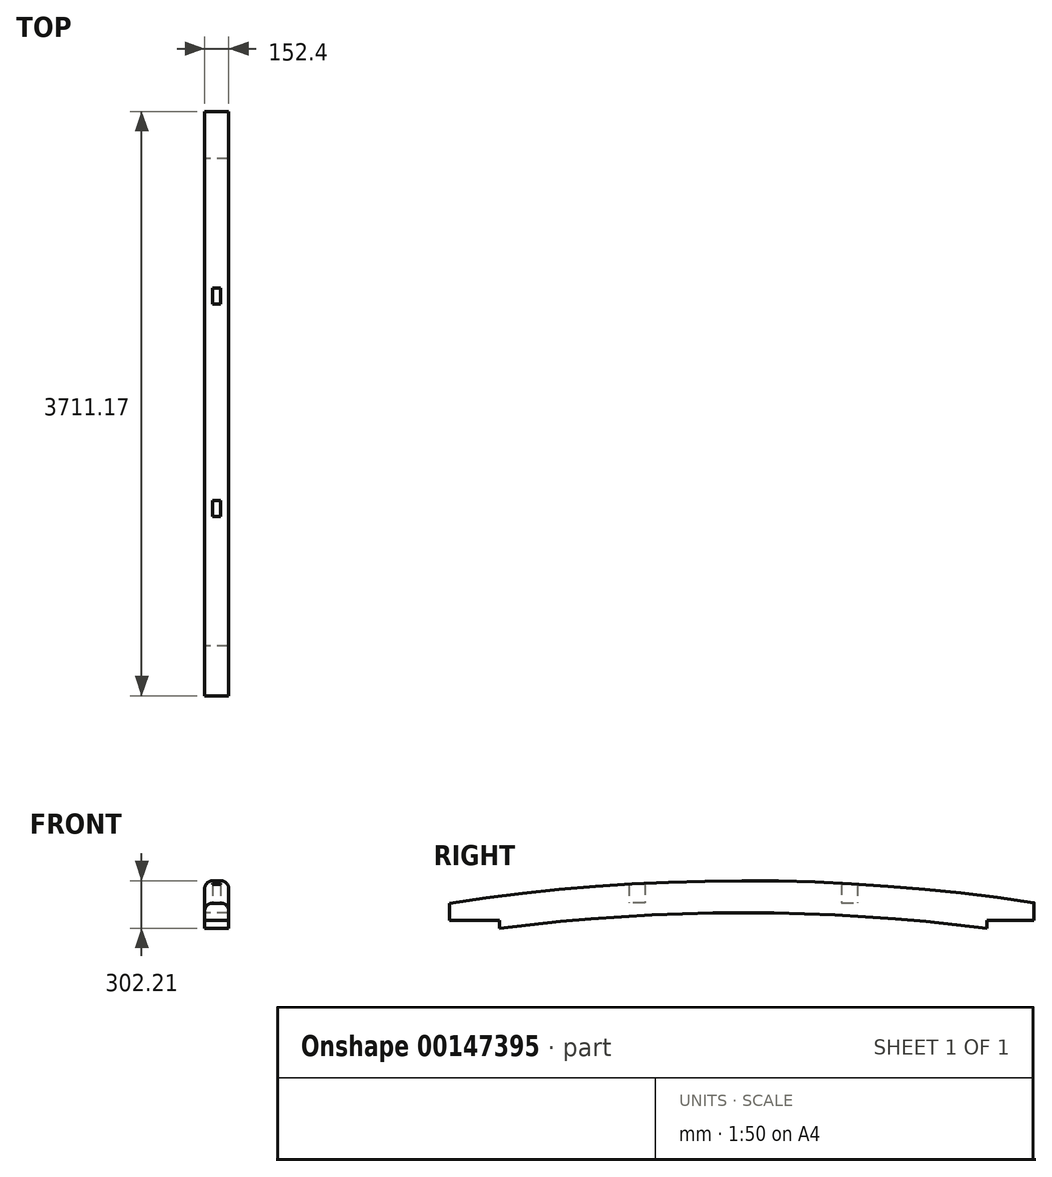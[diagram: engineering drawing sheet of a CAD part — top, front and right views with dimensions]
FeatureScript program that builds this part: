
annotation { "Feature Type Name" : "Feature", "Feature Type Description" : "" }
export const myFeature = defineFeature(function(context is Context, id is Id, definition is map)
    precondition{}
    {
        {
            var Q0;
            Q0=qCreatedBy(makeId("Right.planeOp"),FACE);
            var sketch = newSketch(context, id + "F0", { "sketchPlane" : qUnion([Q0])});
            skLineSegment(sketch, "E0", {"start": v(-1546.8, 0) * mm, "end": v(1546.8, 0) * mm, "construction": true});
            skLineSegment(sketch, "E1.bottom", {"start": v(1546.8, 0) * mm, "end": v(1750, 0) * mm, "construction": true});
            skLineSegment(sketch, "E1.top", {"start": v(1546.8, -203.2) * mm, "end": v(1750, -203.2) * mm, "construction": true});
            skLineSegment(sketch, "E1.left", {"start": v(1546.8, 0) * mm, "end": v(1546.8, -203.2) * mm, "construction": true});
            skLineSegment(sketch, "E1.right", {"start": v(1750, 0) * mm, "end": v(1750, -203.2) * mm, "construction": true});
            skLineSegment(sketch, "E2.bottom", {"start": v(-1546.8, 0) * mm, "end": v(-1750, 0) * mm, "construction": true});
            skLineSegment(sketch, "E2.top", {"start": v(-1546.8, -203.2) * mm, "end": v(-1750, -203.2) * mm, "construction": true});
            skLineSegment(sketch, "E2.left", {"start": v(-1546.8, 0) * mm, "end": v(-1546.8, -203.2) * mm, "construction": true});
            skLineSegment(sketch, "E2.right", {"start": v(-1750, 0) * mm, "end": v(-1750, -203.2) * mm, "construction": true});
            skLineSegment(sketch, "E3.0", {"start": v(-1546.8, -50) * mm, "end": v(1546.8, -50) * mm, "construction": true});
            skArc(sketch, "E4", {"start": v(1546.8, -50) * mm, "mid": v(0, 49.01) * mm, "end": v(-1546.8, -50) * mm});
            skArc(sketch, "E5.0", {"start": v(1846.2, 113.27) * mm, "mid": v(-9.5, 252.2) * mm, "end": v(-1864.97, 110.41) * mm});
            skLineSegment(sketch, "E6", {"start": v(1546.8, -50) * mm, "end": v(1546.8, 0) * mm});
            skLineSegment(sketch, "E7", {"start": v(1846.2, 0) * mm, "end": v(1846.2, 113.27) * mm});
            skLineSegment(sketch, "E8", {"start": v(1846.2, 0) * mm, "end": v(1546.8, 0) * mm});
            skLineSegment(sketch, "E9", {"start": v(-1546.8, -50) * mm, "end": v(-1546.8, 0) * mm});
            skLineSegment(sketch, "E10", {"start": v(-1864.97, 0) * mm, "end": v(-1546.8, 0) * mm});
            skLineSegment(sketch, "E11", {"start": v(-1864.97, 0) * mm, "end": v(-1864.97, 110.41) * mm});
            skLineSegment(sketch, "E12", {"start": v(0, 0) * mm, "end": v(0, -260.57) * mm, "construction": true});
            skSolve(sketch);
        }
        {
            var Q0;
            Q0=makeQuery(id+"F0.imprint","IMPRINT",FACE,{"disambiguationData":[TD([[makeQuery(id+"F0.imprint","IMPRINT",EDGE,{"derivedFrom":sQuery(id+"F0.wireOp",EDGE,"E4")}),-1.0]])]});
            extrude(context, id + "F1", {"entities" : qUnion([Q0]), "depth" : 152.4 * mm});
        }
        {
            var Q0;
            Q0=makeQuery(id+"F1.opExtrude","CAP_EDGE",EDGE,{"disambiguationData":[OSD([sQuery(id+"F0.wireOp",EDGE,"E5.0")])],"isStart":false});
            var Q1;
            Q1=makeQuery(id+"F1.opExtrude","CAP_EDGE",EDGE,{"disambiguationData":[OSD([sQuery(id+"F0.wireOp",EDGE,"E5.0")])],"isStart":true});
            fillet(context, id + "F2", {"entities" : qUnion([Q0, Q1]), "radius" : 50 * mm, "tangentPropagation" : true, "allowEdgeOverflow" : false});
        }
        {
            var Q0;
            {var subQ0=sQuery(id+"F0.wireOp",EDGE,"E5.0");Q0=makeQuery(id+"F2.opFillet","BLEND_VERTEX",VERTEX,{"blendedFrom":[makeQuery(id+"F1.opExtrude","CAP_EDGE",EDGE,{"disambiguationData":[OSD([subQ0])],"isStart":true}),makeQuery(id+"F1.opExtrude","SWEPT_FACE",FACE,{"disambiguationData":[OSD([subQ0])]}),makeQuery(id+"F1.opExtrude","SWEPT_FACE",FACE,{"disambiguationData":[OSD([sQuery(id+"F0.wireOp",EDGE,"E7")])]})],"blendedInto":[makeQuery(id+"F1.opExtrude","SWEPT_FACE",FACE,{"disambiguationData":[OSD([subQ0])]}),makeQuery(id+"F1.opExtrude","SWEPT_FACE",FACE,{"disambiguationData":[OSD([sQuery(id+"F0.wireOp",EDGE,"E7")])]})]});}
            var Q1;
            {var subQ0=sQuery(id+"F0.wireOp",EDGE,"E5.0");Q1=makeQuery(id+"F2.opFillet","BLEND_VERTEX",VERTEX,{"blendedFrom":[makeQuery(id+"F1.opExtrude","CAP_EDGE",EDGE,{"disambiguationData":[OSD([subQ0])],"isStart":false}),makeQuery(id+"F1.opExtrude","SWEPT_FACE",FACE,{"disambiguationData":[OSD([subQ0])]}),makeQuery(id+"F1.opExtrude","SWEPT_FACE",FACE,{"disambiguationData":[OSD([sQuery(id+"F0.wireOp",EDGE,"E7")])]})],"blendedInto":[makeQuery(id+"F1.opExtrude","SWEPT_FACE",FACE,{"disambiguationData":[OSD([subQ0])]}),makeQuery(id+"F1.opExtrude","SWEPT_FACE",FACE,{"disambiguationData":[OSD([sQuery(id+"F0.wireOp",EDGE,"E7")])]})]});}
            var Q2;
            {var subQ0=sQuery(id+"F0.wireOp",EDGE,"E5.0");Q2=makeQuery(id+"F2.opFillet","BLEND_VERTEX",VERTEX,{"blendedFrom":[makeQuery(id+"F1.opExtrude","CAP_EDGE",EDGE,{"disambiguationData":[OSD([subQ0])],"isStart":true}),makeQuery(id+"F1.opExtrude","SWEPT_FACE",FACE,{"disambiguationData":[OSD([subQ0])]}),makeQuery(id+"F1.opExtrude","SWEPT_FACE",FACE,{"disambiguationData":[OSD([sQuery(id+"F0.wireOp",EDGE,"E11")])]})],"blendedInto":[makeQuery(id+"F1.opExtrude","SWEPT_FACE",FACE,{"disambiguationData":[OSD([subQ0])]}),makeQuery(id+"F1.opExtrude","SWEPT_FACE",FACE,{"disambiguationData":[OSD([sQuery(id+"F0.wireOp",EDGE,"E11")])]})]});}
            cPlane(context, id + "F3", {"entities" : qUnion([Q0, Q1, Q2]), "cplaneType" : CPlaneType.THREE_POINT, "offset" : 25 * mm, "width" : 150 * mm, "height" : 150 * mm});
        }
        {
            var Q0;
            Q0=qCreatedBy(id+"F3.planeOp",FACE);
            var sketch = newSketch(context, id + "F4", { "sketchPlane" : qUnion([Q0])});
            skLineSegment(sketch, "E13", {"start": v(504.24, 0) * mm, "end": v(-499.27, 0) * mm, "construction": true});
            skLineSegment(sketch, "E14.bottom", {"start": v(101.6, -625) * mm, "end": v(50.8, -625) * mm});
            skLineSegment(sketch, "E14.top", {"start": v(101.6, -726.6) * mm, "end": v(50.8, -726.6) * mm});
            skLineSegment(sketch, "E14.left", {"start": v(101.6, -625) * mm, "end": v(101.6, -726.6) * mm});
            skLineSegment(sketch, "E14.right", {"start": v(50.8, -625) * mm, "end": v(50.8, -726.6) * mm});
            skLineSegment(sketch, "E15.MirrorCS", {"start": v(101.6, 625) * mm, "end": v(50.8, 625) * mm});
            skLineSegment(sketch, "E16.MirrorCS", {"start": v(101.6, 625) * mm, "end": v(101.6, 726.6) * mm});
            skLineSegment(sketch, "E17.MirrorCS", {"start": v(101.6, 726.6) * mm, "end": v(50.8, 726.6) * mm});
            skLineSegment(sketch, "E18.MirrorCS", {"start": v(50.8, 625) * mm, "end": v(50.8, 726.6) * mm});
            skSolve(sketch);
        }
        {
            var Q0;
            Q0 = qSketchRegion(id + "F4", true);
            extrude(context, id + "F5", {"entities" : qUnion([Q0]), "operationType" : NewBodyOperationType.REMOVE, "depth" : 152.4 * mm});
        }
    });
